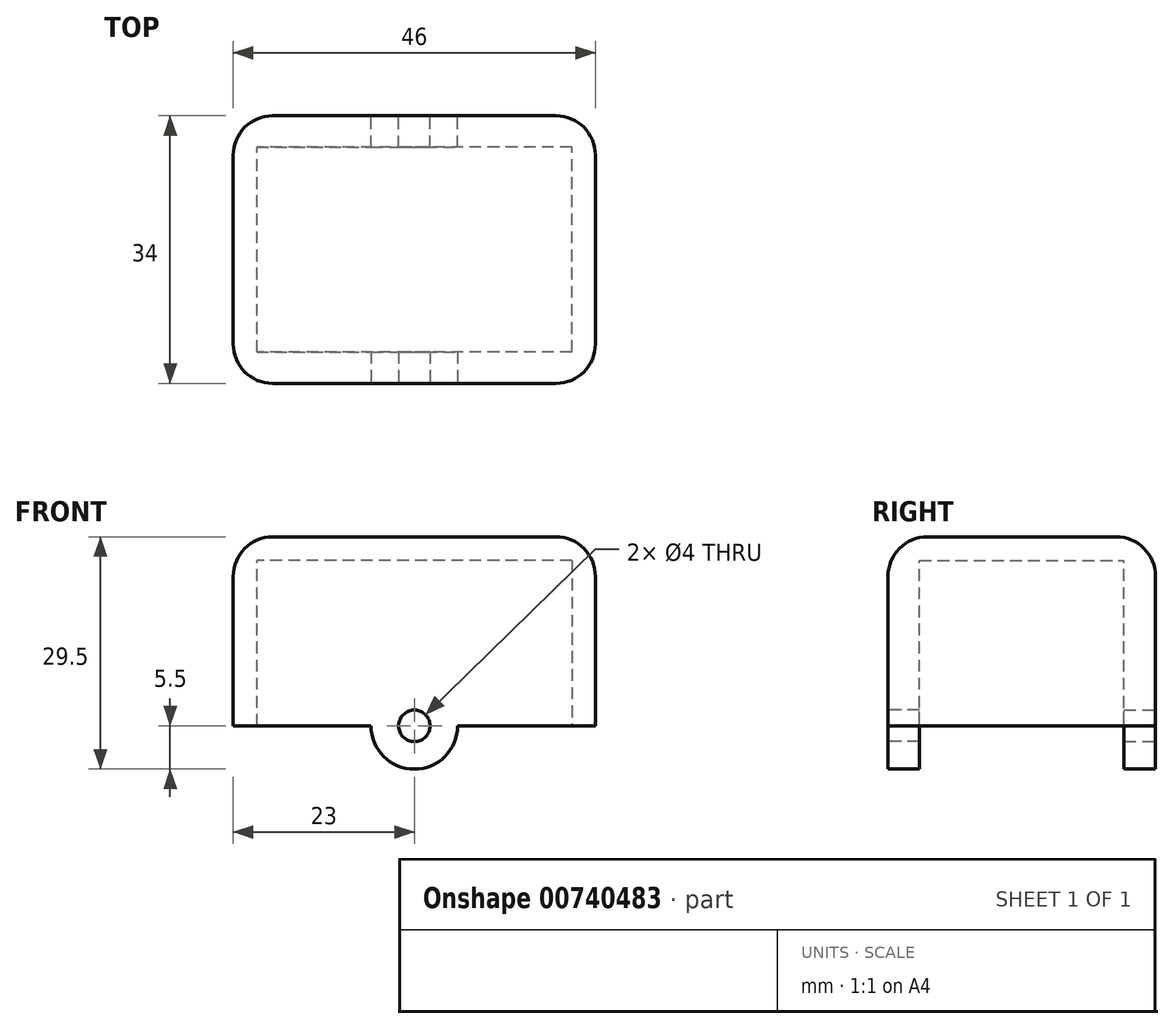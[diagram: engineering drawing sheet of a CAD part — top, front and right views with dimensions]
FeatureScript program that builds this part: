
annotation { "Feature Type Name" : "Feature", "Feature Type Description" : "" }
export const myFeature = defineFeature(function(context is Context, id is Id, definition is map)
    precondition{}
    {
        {
            var Q0;
            Q0=qCreatedBy(makeId("Front.planeOp"),FACE);
            var sketch = newSketch(context, id + "F0", { "sketchPlane" : qUnion([Q0])});
            skLineSegment(sketch, "E0.top", {"start": v(0, 18) * mm, "end": v(40, 18) * mm});
            skLineSegment(sketch, "E0.left", {"start": v(0, 0) * mm, "end": v(0, 18) * mm});
            skLineSegment(sketch, "E0.right", {"start": v(40, 0) * mm, "end": v(40, 18) * mm});
            skLineSegment(sketch, "E1", {"start": v(-3, 21) * mm, "end": v(43, 21) * mm});
            skLineSegment(sketch, "E2", {"start": v(-3, 21) * mm, "end": v(-3, -3) * mm});
            skLineSegment(sketch, "E3", {"start": v(43, 21) * mm, "end": v(43, -3) * mm});
            skLineSegment(sketch, "E4", {"start": v(0, 0) * mm, "end": v(0, -3) * mm});
            skLineSegment(sketch, "E5", {"start": v(40, 0) * mm, "end": v(40, -3) * mm});
            skLineSegment(sketch, "E6", {"start": v(-3, -3) * mm, "end": v(0, -3) * mm});
            skLineSegment(sketch, "E7", {"start": v(43, -3) * mm, "end": v(40, -3) * mm});
            skArc(sketch, "E8.0", {"start": v(14.5, -3) * mm, "mid": v(20, -8.5) * mm, "end": v(25.5, -3) * mm});
            skLineSegment(sketch, "E9.trimOffspring", {"start": v(14.5, -3) * mm, "end": v(0, -3) * mm});
            skLineSegment(sketch, "E10.trimOffspring", {"start": v(25.5, -3) * mm, "end": v(40, -3) * mm});
            skCircle(sketch, "E11", {"center": v(20, -3) * mm, "radius": 2 * mm});
            skSolve(sketch);
        }
        {
            var Q0;
            Q0=makeQuery(id+"F0.imprint","IMPRINT",FACE,{"disambiguationData":[TD([[makeQuery(id+"F0.imprint","IMPRINT",EDGE,{"derivedFrom":sQuery(id+"F0.wireOp",EDGE,"E0.top")}),1.0]])]});
            var Q1;
            Q1=makeQuery(id+"F0.imprint","IMPRINT",FACE,{"disambiguationData":[TD([[makeQuery(id+"F0.imprint","IMPRINT",EDGE,{"derivedFrom":sQuery(id+"F0.wireOp",EDGE,"E0.top")}),-1.0]])]});
            extrude(context, id + "F1", {"entities" : qUnion([Q0, Q1]), "depth" : 4 * mm, "offsetDistance" : 25 * mm});
        }
        {
            var Q0;
            Q0=makeQuery(id+"F0.imprint","IMPRINT",FACE,{"disambiguationData":[TD([[makeQuery(id+"F0.imprint","IMPRINT",EDGE,{"derivedFrom":sQuery(id+"F0.wireOp",EDGE,"E0.top")}),1.0]])]});
            extrude(context, id + "F2", {"entities" : qUnion([Q0]), "operationType" : NewBodyOperationType.ADD, "depth" : 34 * mm, "offsetDistance" : 25 * mm});
        }
        {
            var Q0;
            Q0=makeQuery(id+"F0.imprint","IMPRINT",FACE,{"disambiguationData":[TD([[makeQuery(id+"F0.imprint","IMPRINT",EDGE,{"derivedFrom":sQuery(id+"F0.wireOp",EDGE,"E0.top")}),-1.0]])]});
            cPlane(context, id + "F3", {"entities" : qUnion([Q0]), "cplaneType" : CPlaneType.OFFSET, "offset" : 17 * mm, "width" : 150 * mm, "height" : 150 * mm});
        }
        {
            var Q0;
            Q0=makeQuery(id+"F1.opExtrude","SWEPT_BODY",BODY,{"disambiguationData":[OSD([sQuery(id+"F0.wireOp",EDGE,"E1"),sQuery(id+"F0.wireOp",EDGE,"E2"),sQuery(id+"F0.wireOp",EDGE,"E3"),sQuery(id+"F0.wireOp",EDGE,"E6"),sQuery(id+"F0.wireOp",EDGE,"E7"),sQuery(id+"F0.wireOp",EDGE,"E8.0"),sQuery(id+"F0.wireOp",EDGE,"E9.trimOffspring"),sQuery(id+"F0.wireOp",EDGE,"E10.trimOffspring"),sQuery(id+"F0.wireOp",EDGE,"E11")])]});
            var Q1;
            Q1=qCreatedBy(id+"F3.planeOp",FACE);
            mirror(context, id + "F4", {"operationType" : NewBodyOperationType.ADD, "entities" : qUnion([Q0]), "mirrorPlane" : qUnion([Q1])});
        }
        {
            var Q0;
            Q0=makeQuery(id+"F1.opExtrude","CAP_EDGE",EDGE,{"disambiguationData":[OSD([sQuery(id+"F0.wireOp",EDGE,"E1")])],"isStart":true});
            var Q1;
            {var subQ0=sQuery(id+"F0.wireOp",EDGE,"E2");var subQ1=sQuery(id+"F0.wireOp",EDGE,"E1");Q1=makeQuery(id+"F2.boolean.opBoolean","MERGE",EDGE,{"derivedFrom":[makeQuery(id+"F1.opExtrude","SWEPT_EDGE",EDGE,{"disambiguationData":[OSD([subQ1,subQ0])]}),makeQuery(id+"F2.opExtrude","SWEPT_EDGE",EDGE,{"disambiguationData":[OSD([subQ1,subQ0])]})]});}
            var Q2;
            Q2=makeQuery(id+"F2.opExtrude","CAP_EDGE",EDGE,{"disambiguationData":[OSD([sQuery(id+"F0.wireOp",EDGE,"E1")])],"isStart":false});
            var Q3;
            {var subQ0=sQuery(id+"F0.wireOp",EDGE,"E3");var subQ1=sQuery(id+"F0.wireOp",EDGE,"E1");Q3=makeQuery(id+"F2.boolean.opBoolean","MERGE",EDGE,{"derivedFrom":[makeQuery(id+"F1.opExtrude","SWEPT_EDGE",EDGE,{"disambiguationData":[OSD([subQ1,subQ0])]}),makeQuery(id+"F2.opExtrude","SWEPT_EDGE",EDGE,{"disambiguationData":[OSD([subQ1,subQ0])]})]});}
            var Q4;
            Q4=makeQuery(id+"F1.opExtrude","CAP_EDGE",EDGE,{"disambiguationData":[OSD([sQuery(id+"F0.wireOp",EDGE,"E3")])],"isStart":true});
            var Q5;
            Q5=makeQuery(id+"F1.opExtrude","CAP_EDGE",EDGE,{"disambiguationData":[OSD([sQuery(id+"F0.wireOp",EDGE,"E2")])],"isStart":true});
            var Q6;
            Q6=makeQuery(id+"F2.opExtrude","CAP_EDGE",EDGE,{"disambiguationData":[OSD([sQuery(id+"F0.wireOp",EDGE,"E2")])],"isStart":false});
            var Q7;
            Q7=makeQuery(id+"F2.opExtrude","CAP_EDGE",EDGE,{"disambiguationData":[OSD([sQuery(id+"F0.wireOp",EDGE,"E3")])],"isStart":false});
            fillet(context, id + "F5", {"entities" : qUnion([Q0, Q1, Q2, Q3, Q4, Q5, Q6, Q7]), "radius" : 5 * mm, "tangentPropagation" : true, "allowEdgeOverflow" : false});
        }
    });
